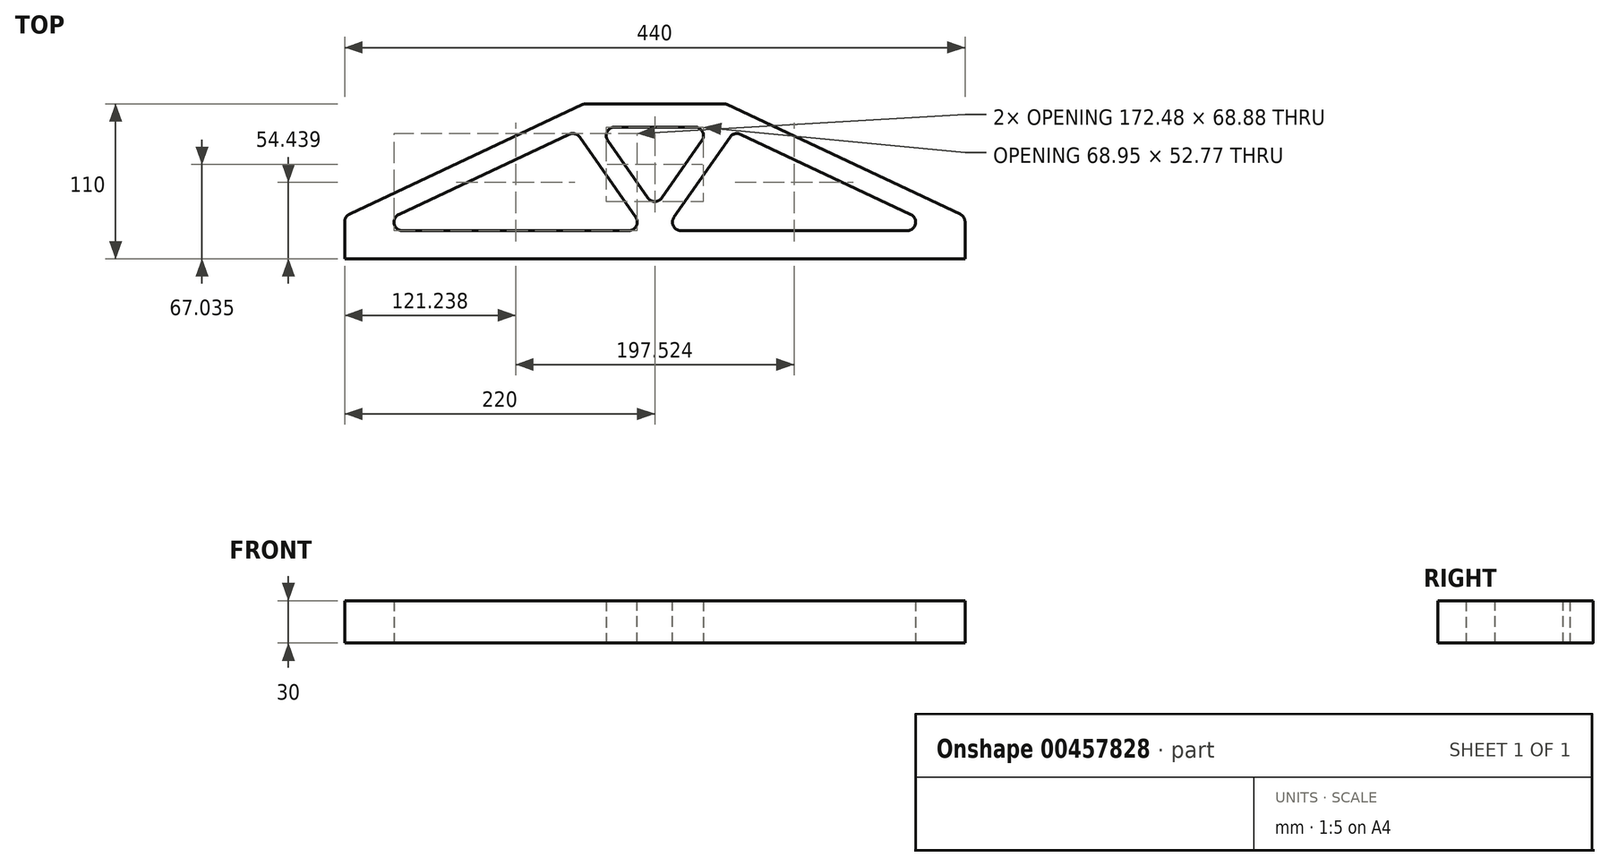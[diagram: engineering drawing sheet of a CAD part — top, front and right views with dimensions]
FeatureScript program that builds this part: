
annotation { "Feature Type Name" : "Feature", "Feature Type Description" : "" }
export const myFeature = defineFeature(function(context is Context, id is Id, definition is map)
    precondition{}
    {
        {
            var Q0;
            Q0=qCreatedBy(makeId("Top.planeOp"),FACE);
            var sketch = newSketch(context, id + "F0", { "sketchPlane" : qUnion([Q0])});
            skLineSegment(sketch, "E0", {"start": v(-220, -50) * mm, "end": v(-220, -20) * mm});
            skLineSegment(sketch, "E1", {"start": v(-220, -20) * mm, "end": v(-50, 60) * mm});
            skLineSegment(sketch, "E2", {"start": v(-50, 60) * mm, "end": v(50, 60) * mm});
            skLineSegment(sketch, "E3", {"start": v(50, 60) * mm, "end": v(220, -20) * mm});
            skLineSegment(sketch, "E4", {"start": v(220, -20) * mm, "end": v(220, -50) * mm});
            skLineSegment(sketch, "E5", {"start": v(220, -50) * mm, "end": v(-220, -50) * mm});
            skSolve(sketch);
        }
        {
            var Q0;
            Q0=makeQuery(id+"F0.imprint","IMPRINT",FACE,{"disambiguationData":[TD([[makeQuery(id+"F0.imprint","IMPRINT",EDGE,{"derivedFrom":sQuery(id+"F0.wireOp",EDGE,"E0")}),-1.0]])]});
            extrude(context, id + "F1", {"entities" : qUnion([Q0]), "depth" : 30 * mm});
        }
        {
            var Q0;
            Q0=makeQuery(id+"F1.opExtrude","CAP_FACE",FACE,{"disambiguationData":[OSD([sQuery(id+"F0.wireOp",EDGE,"E0"),sQuery(id+"F0.wireOp",EDGE,"E1"),sQuery(id+"F0.wireOp",EDGE,"E2"),sQuery(id+"F0.wireOp",EDGE,"E3"),sQuery(id+"F0.wireOp",EDGE,"E4"),sQuery(id+"F0.wireOp",EDGE,"E5")])],"isStart":true});
            var sketch = newSketch(context, id + "F2", { "sketchPlane" : qUnion([Q0])});
            skLineSegment(sketch, "E6", {"start": v(-185, 20.1) * mm, "end": v(-50, -43.42) * mm});
            skLineSegment(sketch, "E7", {"start": v(-50, -43.42) * mm, "end": v(50, -43.42) * mm});
            skLineSegment(sketch, "E8", {"start": v(50, -43.42) * mm, "end": v(185, 20.1) * mm});
            skLineSegment(sketch, "E9", {"start": v(185, 20.1) * mm, "end": v(185, 30) * mm});
            skLineSegment(sketch, "E10", {"start": v(185, 30) * mm, "end": v(-185, 30) * mm});
            skLineSegment(sketch, "E11", {"start": v(-185, 30) * mm, "end": v(-185, 20.1) * mm});
            skPoint(sketch, "E12.end.orphan", {"position": v(0, 30) * mm});
            skLineSegment(sketch, "E13", {"start": v(-56.25, -40.48) * mm, "end": v(-7, 30) * mm});
            skLineSegment(sketch, "E14", {"start": v(-7, 30) * mm, "end": v(7, 30) * mm});
            skLineSegment(sketch, "E15", {"start": v(7, 30) * mm, "end": v(56.25, -40.48) * mm});
            skLineSegment(sketch, "E16", {"start": v(-40, -43.42) * mm, "end": v(-1.28, 12) * mm});
            skLineSegment(sketch, "E17", {"start": v(1.28, 12) * mm, "end": v(40, -43.42) * mm});
            skLineSegment(sketch, "E18", {"start": v(-1.28, 12) * mm, "end": v(0, 13.83) * mm});
            skLineSegment(sketch, "E19", {"start": v(0, 13.83) * mm, "end": v(1.28, 12) * mm});
            skSolve(sketch);
        }
        {
            var Q0;
            Q0=makeQuery(id+"F2.imprint","IMPRINT",FACE,{"disambiguationData":[TD([[makeQuery(id+"F2.imprint","IMPRINT",EDGE,{"derivedFrom":sQuery(id+"F2.wireOp",EDGE,"E6")}),1.0]])]});
            var Q1;
            {var subQ0=sQuery(id+"F2.wireOp",EDGE,"E16");Q1=makeQuery(id+"F2.imprint","IMPRINT",FACE,{"disambiguationData":[TD([[makeQuery(id+"F2.imprint","IMPRINT",EDGE,{"derivedFrom":subQ0}),-1.0]])]});}
            var Q2;
            {var subQ0=sQuery(id+"F2.wireOp",EDGE,"E9");Q2=makeQuery(id+"F2.imprint","IMPRINT",FACE,{"disambiguationData":[TD([[makeQuery(id+"F2.imprint","IMPRINT",EDGE,{"derivedFrom":subQ0}),1.0]])]});}
            extrude(context, id + "F3", {"entities" : qUnion([Q0, Q1, Q2]), "operationType" : NewBodyOperationType.REMOVE, "endBound" : BoundingType.THROUGH_ALL, "oppositeDirection" : true, "depth" : 25.4 * mm});
        }
        {
            var Q0;
            Q0=makeQuery(id+"F3.boolean.opBoolean","COPY",EDGE,{"derivedFrom":makeQuery(id+"F3.opExtrude","SWEPT_EDGE",EDGE,{"disambiguationData":[OSD([sQuery(id+"F2.wireOp",EDGE,"E6"),sQuery(id+"F2.wireOp",EDGE,"E7")])]})});
            var Q1;
            Q1=makeQuery(id+"F3.boolean.opBoolean","COPY",EDGE,{"derivedFrom":makeQuery(id+"F3.opExtrude","SWEPT_EDGE",EDGE,{"disambiguationData":[OSD([sQuery(id+"F2.wireOp",EDGE,"E6"),sQuery(id+"F2.wireOp",EDGE,"E11")])]})});
            var Q2;
            Q2=makeQuery(id+"F3.boolean.opBoolean","COPY",EDGE,{"derivedFrom":makeQuery(id+"F3.opExtrude","SWEPT_EDGE",EDGE,{"disambiguationData":[OSD([sQuery(id+"F2.wireOp",EDGE,"E10"),sQuery(id+"F2.wireOp",EDGE,"E11")])]})});
            var Q3;
            Q3=makeQuery(id+"F3.boolean.opBoolean","COPY",EDGE,{"derivedFrom":makeQuery(id+"F3.opExtrude","SWEPT_EDGE",EDGE,{"disambiguationData":[OSD([sQuery(id+"F2.wireOp",EDGE,"E7"),sQuery(id+"F2.wireOp",EDGE,"E8")])]})});
            var Q4;
            Q4=makeQuery(id+"F3.boolean.opBoolean","COPY",EDGE,{"derivedFrom":makeQuery(id+"F3.opExtrude","SWEPT_EDGE",EDGE,{"disambiguationData":[OSD([sQuery(id+"F2.wireOp",EDGE,"E8"),sQuery(id+"F2.wireOp",EDGE,"E9")])]})});
            var Q5;
            Q5=makeQuery(id+"F3.boolean.opBoolean","COPY",EDGE,{"derivedFrom":makeQuery(id+"F3.opExtrude","SWEPT_EDGE",EDGE,{"disambiguationData":[OSD([sQuery(id+"F2.wireOp",EDGE,"E9"),sQuery(id+"F2.wireOp",EDGE,"E10")])]})});
            var Q6;
            Q6=makeQuery(id+"F1.opExtrude","SWEPT_EDGE",EDGE,{"disambiguationData":[OSD([sQuery(id+"F0.wireOp",EDGE,"E1"),sQuery(id+"F0.wireOp",EDGE,"E2")])]});
            var Q7;
            Q7=makeQuery(id+"F1.opExtrude","SWEPT_EDGE",EDGE,{"disambiguationData":[OSD([sQuery(id+"F0.wireOp",EDGE,"E2"),sQuery(id+"F0.wireOp",EDGE,"E3")])]});
            var Q8;
            Q8=makeQuery(id+"F1.opExtrude","SWEPT_EDGE",EDGE,{"disambiguationData":[OSD([sQuery(id+"F0.wireOp",EDGE,"E3"),sQuery(id+"F0.wireOp",EDGE,"E4")])]});
            var Q9;
            Q9=makeQuery(id+"F1.opExtrude","SWEPT_EDGE",EDGE,{"disambiguationData":[OSD([sQuery(id+"F0.wireOp",EDGE,"E0"),sQuery(id+"F0.wireOp",EDGE,"E1")])]});
            var Q10;
            Q10=makeQuery(id+"F3.boolean.opBoolean","COPY",EDGE,{"derivedFrom":makeQuery(id+"F3.opExtrude","SWEPT_EDGE",EDGE,{"disambiguationData":[OSD([sQuery(id+"F2.wireOp",EDGE,"E10"),sQuery(id+"F2.wireOp",EDGE,"E13"),sQuery(id+"F2.wireOp",EDGE,"E14")])]})});
            var Q11;
            Q11=makeQuery(id+"F3.boolean.opBoolean","COPY",EDGE,{"derivedFrom":makeQuery(id+"F3.opExtrude","SWEPT_EDGE",EDGE,{"disambiguationData":[OSD([sQuery(id+"F2.wireOp",EDGE,"E10"),sQuery(id+"F2.wireOp",EDGE,"E14"),sQuery(id+"F2.wireOp",EDGE,"E15")])]})});
            var Q12;
            Q12=makeQuery(id+"F3.boolean.opBoolean","COPY",EDGE,{"derivedFrom":makeQuery(id+"F3.opExtrude","SWEPT_EDGE",EDGE,{"disambiguationData":[OSD([sQuery(id+"F2.wireOp",EDGE,"E18"),sQuery(id+"F2.wireOp",EDGE,"E19")])]})});
            fillet(context, id + "F4", {"entities" : qUnion([Q0, Q1, Q2, Q3, Q4, Q5, Q6, Q7, Q8, Q9, Q10, Q11, Q12]), "radius" : 6 * mm, "tangentPropagation" : true, "allowEdgeOverflow" : false});
        }
    });
